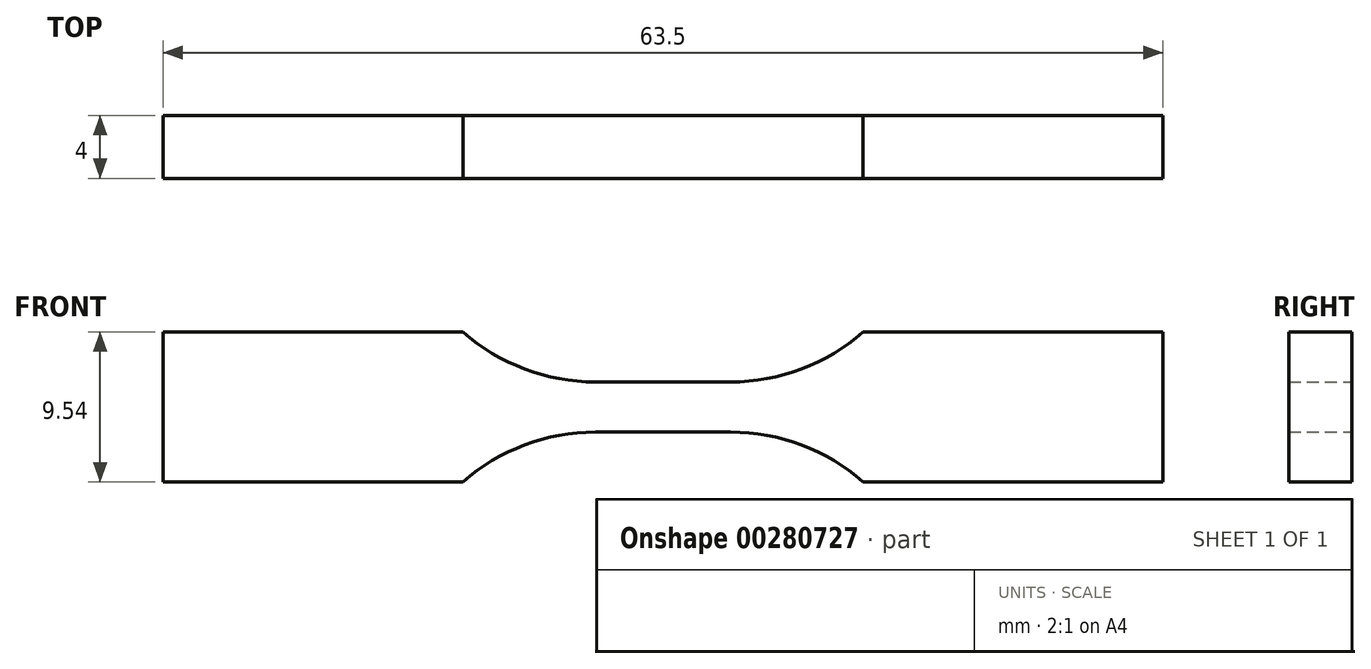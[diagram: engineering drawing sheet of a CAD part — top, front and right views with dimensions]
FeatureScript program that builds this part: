
annotation { "Feature Type Name" : "Feature", "Feature Type Description" : "" }
export const myFeature = defineFeature(function(context is Context, id is Id, definition is map)
    precondition{}
    {
        {
            var Q0;
            Q0=qCreatedBy(makeId("Front.planeOp"),FACE);
            var sketch = newSketch(context, id + "F0", { "sketchPlane" : qUnion([Q0])});
            skLineSegment(sketch, "E0", {"start": v(0, 1.6) * mm, "end": v(4.3, 1.6) * mm});
            skArc(sketch, "E1", {"start": v(4.3, 1.6) * mm, "mid": v(8.79, 2.41) * mm, "end": v(12.7, 4.76) * mm});
            skLineSegment(sketch, "E2", {"start": v(12.7, 4.76) * mm, "end": v(31.75, 4.76) * mm});
            skLineSegment(sketch, "E3", {"start": v(31.75, 4.77) * mm, "end": v(31.75, 0) * mm});
            skLineSegment(sketch, "E4.MirrorCS", {"start": v(0, -1.59) * mm, "end": v(4.3, -1.59) * mm});
            skLineSegment(sketch, "E5.MirrorCS", {"start": v(31.75, -4.77) * mm, "end": v(31.75, 0) * mm});
            skLineSegment(sketch, "E6.MirrorCS", {"start": v(12.7, -4.77) * mm, "end": v(31.75, -4.77) * mm});
            skArc(sketch, "E7.MirrorCS", {"start": v(4.3, -1.6) * mm, "mid": v(8.79, -2.41) * mm, "end": v(12.7, -4.76) * mm});
            skArc(sketch, "E8.MirrorCS", {"start": v(-4.3, -1.6) * mm, "mid": v(-8.79, -2.41) * mm, "end": v(-12.7, -4.76) * mm});
            skLineSegment(sketch, "E9.MirrorCS", {"start": v(-12.7, -4.76) * mm, "end": v(-31.75, -4.77) * mm});
            skArc(sketch, "E10.MirrorCS", {"start": v(-4.3, 1.6) * mm, "mid": v(-8.79, 2.41) * mm, "end": v(-12.7, 4.76) * mm});
            skLineSegment(sketch, "E11.MirrorCS", {"start": v(-12.7, 4.77) * mm, "end": v(-31.75, 4.76) * mm});
            skLineSegment(sketch, "E12.MirrorCS", {"start": v(-31.75, -4.77) * mm, "end": v(-31.75, 0) * mm});
            skLineSegment(sketch, "E13.MirrorCS", {"start": v(0, -1.59) * mm, "end": v(-4.3, -1.59) * mm});
            skLineSegment(sketch, "E14.MirrorCS", {"start": v(-31.75, 4.77) * mm, "end": v(-31.75, 0) * mm});
            skLineSegment(sketch, "E15.MirrorCS", {"start": v(0, 1.6) * mm, "end": v(-4.3, 1.6) * mm});
            skSolve(sketch);
        }
        {
            var Q0;
            Q0 = qSketchRegion(id + "F0", true);
            extrude(context, id + "F1", {"entities" : qUnion([Q0]), "endBound" : BoundingType.SYMMETRIC, "depth" : 4 * mm});
        }
    });
